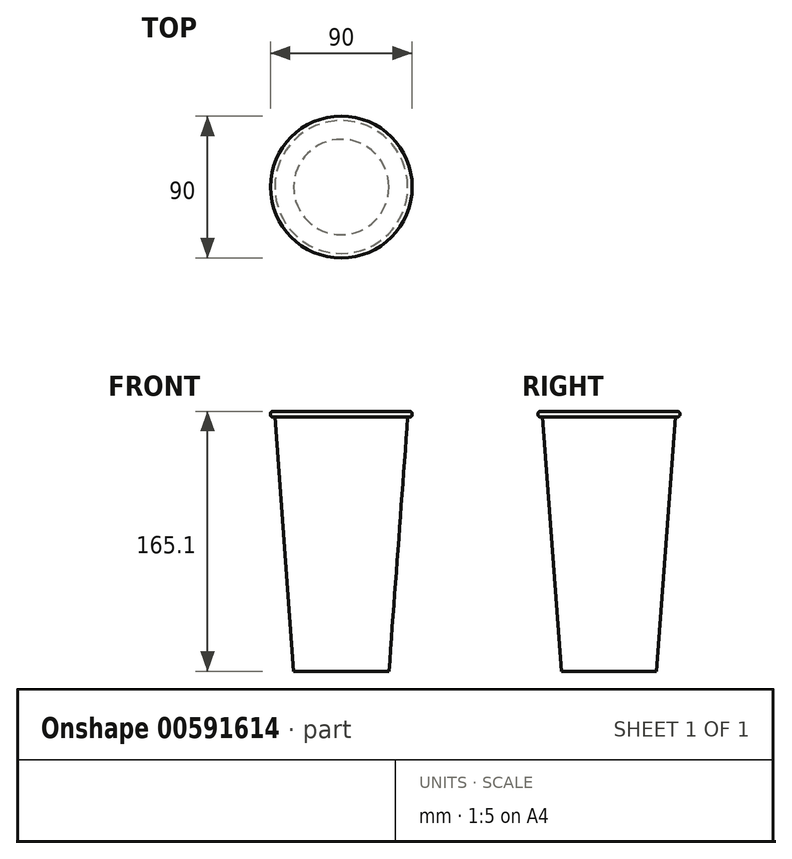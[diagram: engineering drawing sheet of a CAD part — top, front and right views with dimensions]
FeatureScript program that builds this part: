
annotation { "Feature Type Name" : "Feature", "Feature Type Description" : "" }
export const myFeature = defineFeature(function(context is Context, id is Id, definition is map)
    precondition{}
    {
        {
            var Q0;
            Q0=qCreatedBy(makeId("Front.planeOp"),FACE);
            var sketch = newSketch(context, id + "F0", { "sketchPlane" : qUnion([Q0])});
            skPoint(sketch, "E0.left.start.orphan", {"position": v(-57.76, 111) * mm});
            skPoint(sketch, "E1.orphan", {"position": v(-66.13, -50.5) * mm});
            skPoint(sketch, "E0.right.end.orphan", {"position": v(35.02, -50.5) * mm});
            skLineSegment(sketch, "E2", {"start": v(26.64, 111) * mm, "end": v(14.74, -50.5) * mm});
            skPoint(sketch, "E0.top.end.orphan", {"position": v(0, -50.5) * mm});
            skLineSegment(sketch, "E3", {"start": v(-15.56, -50.5) * mm, "end": v(14.74, -50.5) * mm});
            skLineSegment(sketch, "E4.top", {"start": v(-15.56, 114.6) * mm, "end": v(28, 114.6) * mm});
            skPoint(sketch, "E5.visualSharp", {"position": v(29.44, 114.6) * mm});
            skArc(sketch, "E5.filletArc", {"start": v(29.44, 113.16) * mm, "mid": v(29.02, 114.18) * mm, "end": v(28, 114.6) * mm});
            skPoint(sketch, "E6.visualSharp", {"position": v(29.44, 111) * mm});
            skArc(sketch, "E6.filletArc", {"start": v(28, 111) * mm, "mid": v(29.02, 111.42) * mm, "end": v(29.44, 112.44) * mm});
            skPoint(sketch, "E4.left.start.orphan", {"position": v(-15.56, 111) * mm});
            skLineSegment(sketch, "E7", {"start": v(-15.56, 114.6) * mm, "end": v(-15.56, -50.5) * mm});
            skLineSegment(sketch, "E8", {"start": v(29.44, 113.16) * mm, "end": v(29.44, 112.44) * mm});
            skLineSegment(sketch, "E9", {"start": v(28, 111) * mm, "end": v(26.64, 111) * mm});
            skSolve(sketch);
        }
        {
            var Q0;
            Q0 = qSketchRegion(id + "F0", true);
            var Q1;
            Q1=sQuery(id+"F0.wireOp",EDGE,"E7");
            revolve(context, id + "F1", {"entities" : qUnion([Q0]), "axis" : qUnion([Q1]), "revolveType" : RevolveType.FULL});
        }
    });
